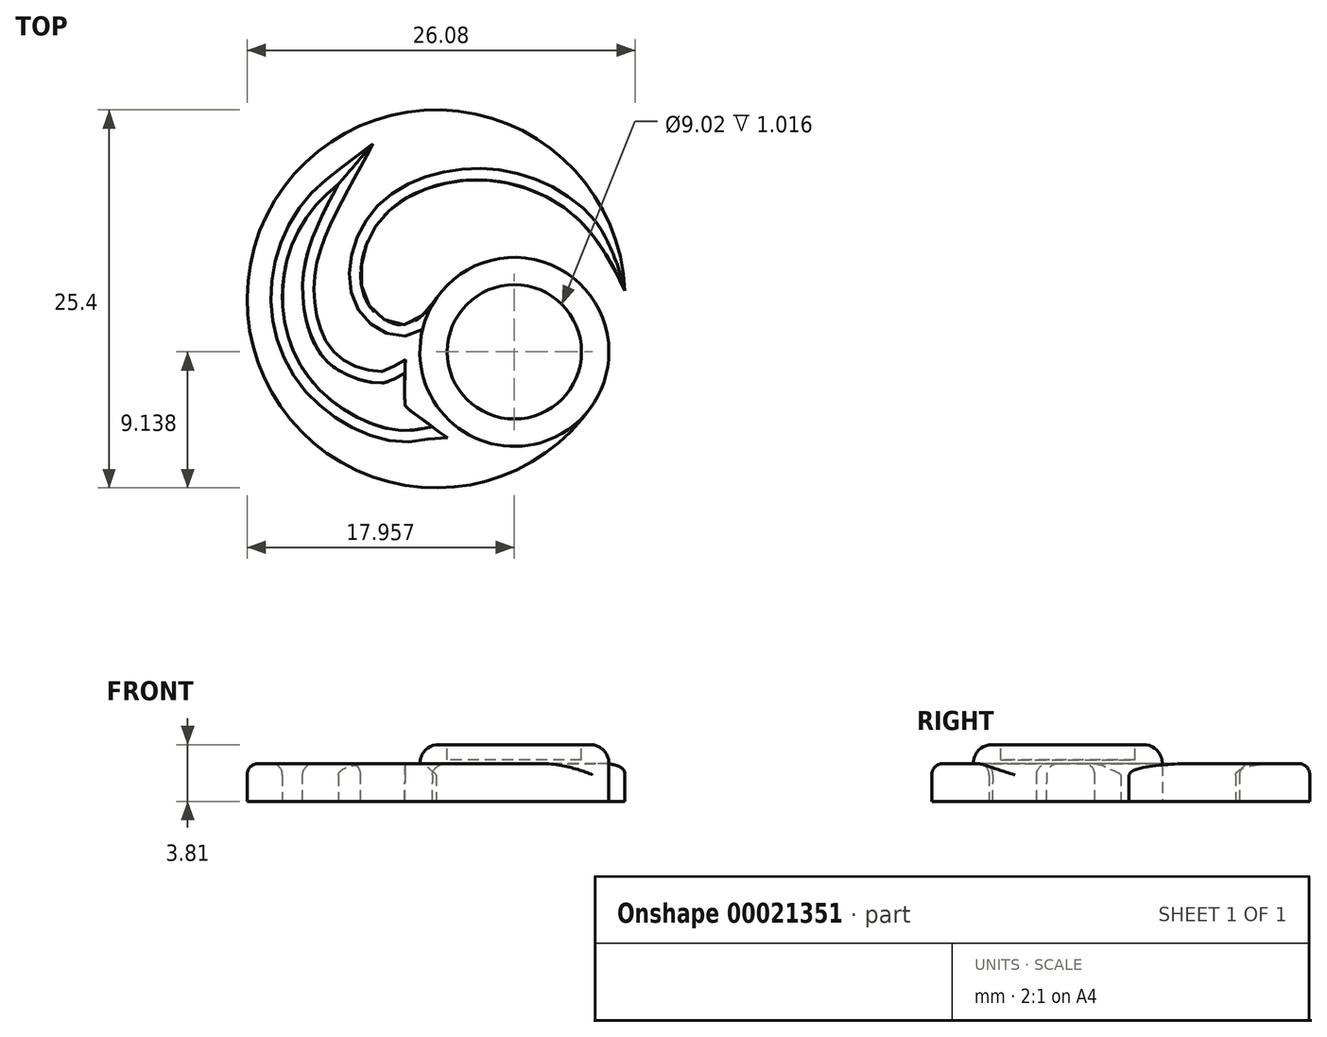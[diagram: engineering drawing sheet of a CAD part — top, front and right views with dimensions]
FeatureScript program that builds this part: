
annotation { "Feature Type Name" : "Feature", "Feature Type Description" : "" }
export const myFeature = defineFeature(function(context is Context, id is Id, definition is map)
    precondition{}
    {
        {
            var Q0;
            Q0=qCreatedBy(makeId("Top.planeOp"),FACE);
            var sketch = newSketch(context, id + "F0", { "sketchPlane" : qUnion([Q0])});
            skCircle(sketch, "E0", {"center": v(0, 0) * mm, "radius": 12.7 * mm});
            skSolve(sketch);
        }
        {
            var Q0;
            Q0 = qSketchRegion(id + "F0", true);
            extrude(context, id + "F1", {"entities" : qUnion([Q0]), "depth" : 1.27 * mm});
        }
        {
            var Q0;
            Q0=makeQuery(id+"F1.opExtrude","CAP_FACE",FACE,{"disambiguationData":[OSD([sQuery(id+"F0.wireOp",EDGE,"E0")])],"isStart":false});
            var sketch = newSketch(context, id + "F2", { "sketchPlane" : qUnion([Q0])});
            skCircle(sketch, "E1", {"center": v(5.26, -3.56) * mm, "radius": 6.35 * mm});
            skFitSpline(sketch, "E2", {"points": [v(0, 0) * mm, v(-3.01, -1.6) * mm, v(-4.76, 0) * mm, v(-4.76, 3.42) * mm, v(-2.34, 6.57) * mm, v(2.6, 8) * mm, v(7.31, 6.9) * mm, v(12.69, 0.55) * mm], "startDerivative": vector(-30.07, -43.3) * mm, "endDerivative": vector(27.4, -59.65) * mm});
            skCircle(sketch, "E3", {"center": v(0, 0) * mm, "radius": 12.7 * mm});
            skFitSpline(sketch, "E4", {"points": [v(-6.57, 7.71) * mm, v(-10.33, 0) * mm, v(-7.76, -6.18) * mm, v(-2.34, -8.85) * mm, v(-0.25, -8.6) * mm], "startDerivative": vector(-26.64, -20.12) * mm, "endDerivative": vector(7.5, 0.18) * mm});
            skFitSpline(sketch, "E5", {"points": [v(-6.57, 7.71) * mm, v(-8.97, 0.79) * mm, v(-7.33, -4.2) * mm, v(-4.15, -5.63) * mm, v(-2.1, -4.99) * mm], "startDerivative": vector(-15.18, -28.19) * mm, "endDerivative": vector(19.1, 10.96) * mm});
            skFitSpline(sketch, "E6", {"points": [v(-2.1, -4.99) * mm, v(-2.1, -6.98) * mm, v(-0.25, -8.6) * mm], "startDerivative": vector(-0.27, -7.67) * mm, "endDerivative": vector(10.52, -7.69) * mm});
            skSolve(sketch);
        }
        {
            var Q0;
            {var subQ3=sQuery(id+"F2.wireOp",EDGE,"E2");Q0=makeQuery(id+"F2.imprint","IMPRINT",FACE,{"disambiguationData":[TD([[makeQuery(id+"F2.imprint","IMPRINT",EDGE,{"derivedFrom":subQ3}),1.0]])]});}
            extrude(context, id + "F3", {"entities" : qUnion([Q0]), "operationType" : NewBodyOperationType.ADD, "depth" : 1.27 * mm});
        }
        {
            var Q0;
            {var subQ0=sQuery(id+"F0.wireOp",EDGE,"E0");Q0=makeQuery(id+"F3.boolean.opBoolean","SPLIT",FACE,{"disambiguationData":[TD([makeQuery(id+"F1.opExtrude","SWEPT_FACE",FACE,{"disambiguationData":[OSD([subQ0])]})])],"derivedFrom":makeQuery(id+"F1.opExtrude","CAP_FACE",FACE,{"disambiguationData":[OSD([subQ0])],"isStart":false})});}
            var sketch = newSketch(context, id + "F4", { "sketchPlane" : qUnion([Q0])});
            skCircle(sketch, "E7", {"center": v(5.26, -3.56) * mm, "radius": 6.35 * mm});
            skPoint(sketch, "E7.first.point", {"position": v(0, 0) * mm});
            skPoint(sketch, "E7.second.point", {"position": v(1.7, -8.82) * mm});
            skPoint(sketch, "E7.third.point", {"position": v(7.42, -9.53) * mm});
            skSolve(sketch);
        }
        {
            var Q0;
            Q0 = qSketchRegion(id + "F4", true);
            extrude(context, id + "F5", {"entities" : qUnion([Q0]), "operationType" : NewBodyOperationType.ADD, "depth" : 2.54 * mm});
        }
        {
            var Q0;
            Q0=makeQuery(id+"F3.opExtrude","CAP_EDGE",EDGE,{"disambiguationData":[OSD([sQuery(id+"F2.wireOp",EDGE,"E3")])],"isStart":false});
            var Q1;
            Q1=makeQuery(id+"F3.opExtrude","CAP_EDGE",EDGE,{"disambiguationData":[OSD([sQuery(id+"F2.wireOp",EDGE,"E2")])],"isStart":false});
            var Q2;
            Q2=makeQuery(id+"F3.opExtrude","CAP_EDGE",EDGE,{"disambiguationData":[OSD([sQuery(id+"F2.wireOp",EDGE,"E5")])],"isStart":false});
            var Q3;
            Q3=makeQuery(id+"F3.opExtrude","CAP_EDGE",EDGE,{"disambiguationData":[OSD([sQuery(id+"F2.wireOp",EDGE,"E4")])],"isStart":false});
            fillet(context, id + "F6", {"entities" : qUnion([Q0, Q1, Q2, Q3]), "radius" : 0.76 * mm, "tangentPropagation" : true, "allowEdgeOverflow" : false});
        }
        {
            var Q0;
            Q0=makeQuery(id+"F5.opExtrude","CAP_EDGE",EDGE,{"disambiguationData":[OSD([sQuery(id+"F4.wireOp",EDGE,"E7")])],"isStart":false});
            fillet(context, id + "F7", {"entities" : qUnion([Q0]), "radius" : 1.27 * mm, "tangentPropagation" : true, "allowEdgeOverflow" : false});
        }
        {
            var Q0;
            Q0=makeQuery(id+"F3.boolean.opBoolean","SPLIT",FACE,{"disambiguationData":[TD([makeQuery(id+"F3.opExtrude","SWEPT_FACE",FACE,{"disambiguationData":[OSD([sQuery(id+"F2.wireOp",EDGE,"E4")])]})])],"derivedFrom":makeQuery(id+"F1.opExtrude","CAP_FACE",FACE,{"disambiguationData":[OSD([sQuery(id+"F0.wireOp",EDGE,"E0")])],"isStart":false})});
            extrude(context, id + "F8", {"entities" : qUnion([Q0]), "operationType" : NewBodyOperationType.REMOVE, "oppositeDirection" : true, "depth" : 25.4 * mm});
        }
        {
            var Q0;
            {var subQ0=sQuery(id+"F0.wireOp",EDGE,"E0");Q0=makeQuery(id+"F3.boolean.opBoolean","SPLIT",FACE,{"disambiguationData":[TD([makeQuery(id+"F1.opExtrude","SWEPT_FACE",FACE,{"disambiguationData":[OSD([subQ0])]})])],"derivedFrom":makeQuery(id+"F1.opExtrude","CAP_FACE",FACE,{"disambiguationData":[OSD([subQ0])],"isStart":false})});}
            extrude(context, id + "F9", {"entities" : qUnion([Q0]), "operationType" : NewBodyOperationType.REMOVE, "oppositeDirection" : true, "depth" : 25.4 * mm});
        }
        {
            var Q0;
            Q0=makeQuery(id+"F5.opExtrude","CAP_FACE",FACE,{"disambiguationData":[OSD([sQuery(id+"F4.wireOp",EDGE,"E7")])],"isStart":false});
            var sketch = newSketch(context, id + "F10", { "sketchPlane" : qUnion([Q0])});
            skCircle(sketch, "E8", {"center": v(5.26, -3.56) * mm, "radius": 4.51 * mm});
            skSolve(sketch);
        }
        {
            var Q0;
            Q0 = qSketchRegion(id + "F10", true);
            extrude(context, id + "F11", {"entities" : qUnion([Q0]), "operationType" : NewBodyOperationType.REMOVE, "oppositeDirection" : true, "depth" : 1.02 * mm});
        }
    });
